# Revit family: Pantalla Modelo Cortina ligera_LPGM16.2
name_source: partatom
category: Luminarias
units: mm (PartAtom-declared; Revit-internal decimal feet)

## family parameters
Compartido = No
Corte con vacíos al cargar = No
Cota de conector redondo = Diámetro de uso
Origen de luz = No
Punto de cálculo de habitación = No
Se basa en plano de trabajo = Sí
Siempre vertical = No
Tipo de pieza = Normal

## types (1)
- Pantalla Modelo Cortina ligera_LPGM16.2
    Comentarios de vataje = 90-264V
    Descripción = PANTALLA MODELO CORTINA LIGERA CON UNA INTERFAZ BASE A TIRA LED, PINS, PANEL, CONECTORES, MODO DE INSTALACION FIJA, PITCH DE 16X16, TAMAÑO DEL PANEL DE 1024X1024X78MM, DENSIDAD DE PIXELES DE 3906 PIXEL/M2, LUMINOSIDAD 6000 CD/M2, CONFIGURACION DE PIXEL 1R 1G 1B, TIPO DE LED DIP 346, PROFUNDIDAD DE PROCESAMIENTO 14BIT, VELOCIDAD DE ACTUALIZACION 1920Hz, 10000 HRS DE VIDA PROMEDIO, LED TIRA FRONTAL IP67 Y CAJA DE CONTROL IP66, CONSUMO PROMEDIO 190W/M2 Y MAXIMO 540W/M2, TEMPERATURA DE ALMACENAMIENTO -40 A +60C, HUMEDAD DE ALMACENAMIENTO 10-90%, MODO DE PROTECCION COMPLETA CONTRA ROCIADURAS, TORNILLERIA INOXIDABLE, TEMPERATURA DE COLOR 6500 MAS MENOS 300K (3200-9300K AJUSTABLE), FUENTE DE ALIMENTACION AUTOAJUSTABLE DE ALTA EFICIENCIA 90-264VAC, VOLTAJE DE MODULO 5V, PRUEBA DE TENSION DE 1500V/1 MINUTO O 3000V/1SEGUNDO, RESISTENCIA EN 4 OHMS, CORRIENTE DE FUGA 3.5mA, MODO DE CONDUCCION ESTATICO, MODO DE TRABAJO CONTINUO, PESO DE 22KG/M2, BRECHA CONJUNTA DE MAS MENOS 1MM, TRANSPARENCIA DE 21.3%/25.2MM. REQUIERE ACCESORIOS COMO: CABLE DE ENTRADA DE SEÑAL, CABLE DE ENTRADA DE ENERGIA, PLACA DE CONEXIÓN Y PUNTO DE MONTAJE.
    Elevación por defecto = 0 mm  [stored 0 ft]
    Espesor = 78 mm
    Fabricante = BRILLANT
    Lámpara = DIP 346
    Modelo = LPGM16.2
    Modulo = 320 mm
    Watt per fixture = 540

note: [stored X ft] marks values corroborated as IEEE doubles in the binary element streams (Revit-internal decimal feet)

## geometry (parser evidence)
native form markers: Blend x2
no freeform markers — native parametric forms only
